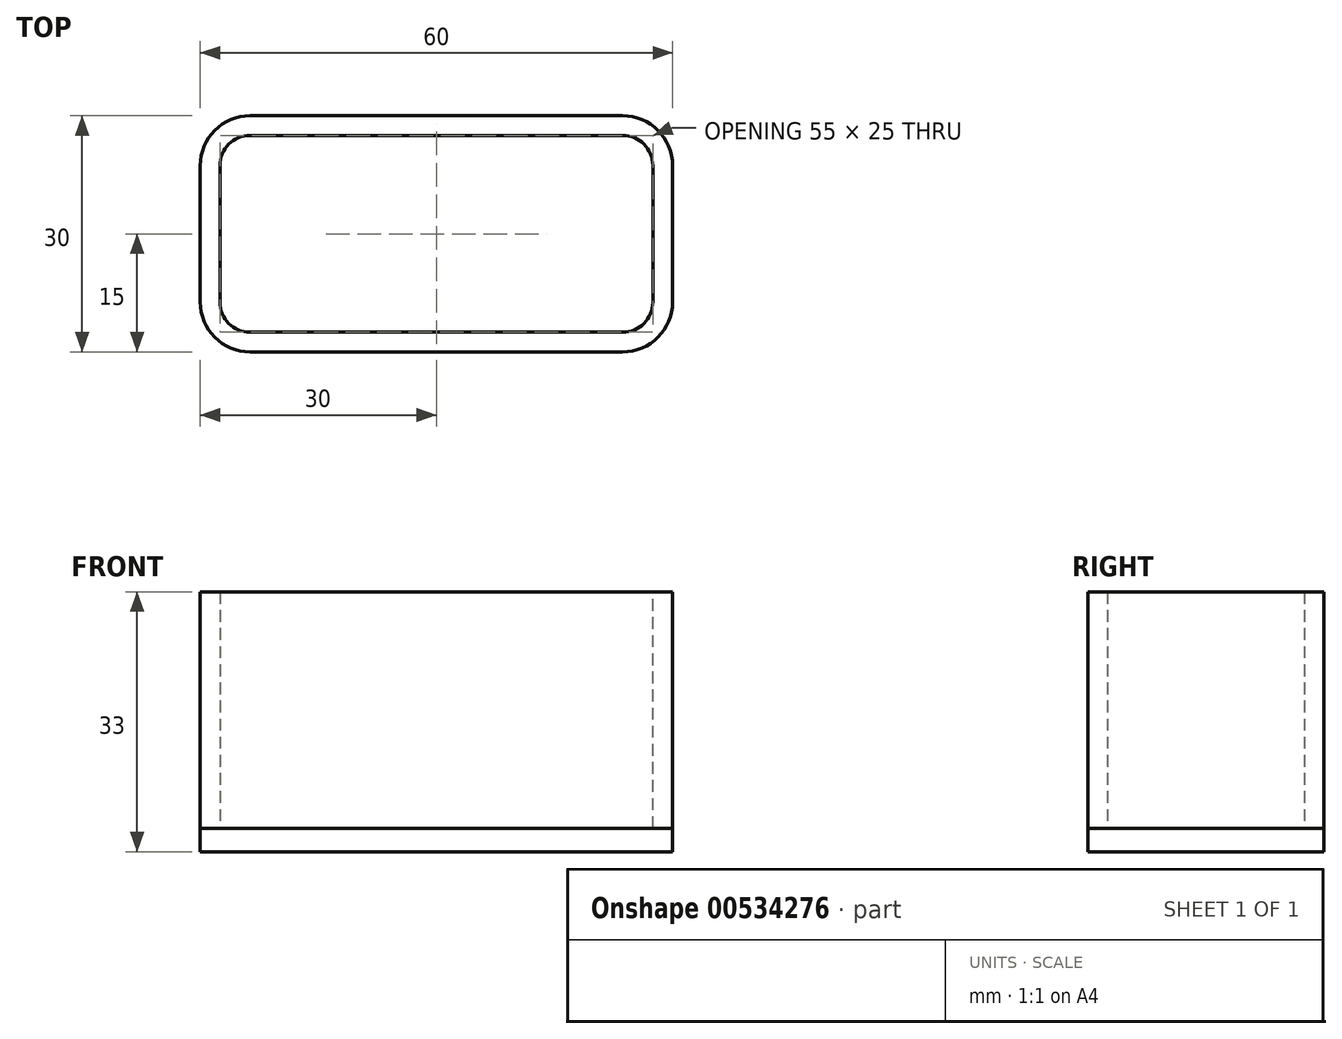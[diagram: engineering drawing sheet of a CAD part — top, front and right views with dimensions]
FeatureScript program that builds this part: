
annotation { "Feature Type Name" : "Feature", "Feature Type Description" : "" }
export const myFeature = defineFeature(function(context is Context, id is Id, definition is map)
    precondition{}
    {
        {
            var Q0;
            Q0=qCreatedBy(makeId("Top.planeOp"),FACE);
            var sketch = newSketch(context, id + "F0", { "sketchPlane" : qUnion([Q0])});
            skLineSegment(sketch, "E0.bottom", {"start": v(23.65, -15) * mm, "end": v(-23.65, -15) * mm});
            skLineSegment(sketch, "E0.top", {"start": v(23.65, 15) * mm, "end": v(-23.65, 15) * mm});
            skLineSegment(sketch, "E0.left", {"start": v(30, -8.65) * mm, "end": v(30, 8.65) * mm});
            skLineSegment(sketch, "E0.right", {"start": v(-30, -8.65) * mm, "end": v(-30, 8.65) * mm});
            skPoint(sketch, "E0.middle", {"position": v(0, 0) * mm});
            skPoint(sketch, "E1.visualSharp", {"position": v(-30, 15) * mm});
            skArc(sketch, "E1.filletArc", {"start": v(-23.65, 15) * mm, "mid": v(-28.14, 13.14) * mm, "end": v(-30, 8.65) * mm});
            skPoint(sketch, "E2.visualSharp", {"position": v(-30, -15) * mm});
            skArc(sketch, "E2.filletArc", {"start": v(-30, -8.65) * mm, "mid": v(-28.14, -13.14) * mm, "end": v(-23.65, -15) * mm});
            skPoint(sketch, "E3.visualSharp", {"position": v(30, -15) * mm});
            skArc(sketch, "E3.filletArc", {"start": v(23.65, -15) * mm, "mid": v(28.14, -13.14) * mm, "end": v(30, -8.65) * mm});
            skPoint(sketch, "E4.visualSharp", {"position": v(30, 15) * mm});
            skArc(sketch, "E4.filletArc", {"start": v(30, 8.65) * mm, "mid": v(28.14, 13.14) * mm, "end": v(23.65, 15) * mm});
            skSolve(sketch);
        }
        {
            var Q0;
            Q0=makeQuery(id+"F0.imprint","IMPRINT",FACE,{"disambiguationData":[TD([[makeQuery(id+"F0.imprint","IMPRINT",EDGE,{"derivedFrom":sQuery(id+"F0.wireOp",EDGE,"E0.bottom")}),-1.0]])]});
            extrude(context, id + "F1", {"entities" : qUnion([Q0]), "depth" : 30 * mm, "offsetDistance" : 25 * mm});
        }
        {
            var Q0;
            Q0=makeQuery(id+"F1.opExtrude","CAP_FACE",FACE,{"disambiguationData":[OSD([sQuery(id+"F0.wireOp",EDGE,"E0.bottom"),sQuery(id+"F0.wireOp",EDGE,"E0.top"),sQuery(id+"F0.wireOp",EDGE,"E0.left"),sQuery(id+"F0.wireOp",EDGE,"E0.right"),sQuery(id+"F0.wireOp",EDGE,"E1.filletArc"),sQuery(id+"F0.wireOp",EDGE,"E2.filletArc"),sQuery(id+"F0.wireOp",EDGE,"E3.filletArc"),sQuery(id+"F0.wireOp",EDGE,"E4.filletArc")])],"isStart":false});
            shell(context, id + "F2", {"entities" : qUnion([Q0]), "thickness" : 2.5 * mm});
        }
        {
            var Q0;
            Q0=makeQuery(id+"F2.opShell","OFFSET_FACE",FACE,{"disambiguationData":[OSD([sQuery(id+"F0.wireOp",EDGE,"E0.bottom"),sQuery(id+"F0.wireOp",EDGE,"E0.top"),sQuery(id+"F0.wireOp",EDGE,"E0.left"),sQuery(id+"F0.wireOp",EDGE,"E0.right"),sQuery(id+"F0.wireOp",EDGE,"E1.filletArc"),sQuery(id+"F0.wireOp",EDGE,"E2.filletArc"),sQuery(id+"F0.wireOp",EDGE,"E3.filletArc"),sQuery(id+"F0.wireOp",EDGE,"E4.filletArc")])]});
            var sketch = newSketch(context, id + "F3", { "sketchPlane" : qUnion([Q0])});
            skArc(sketch, "E5.0.0", {"start": v(27.5, 8.65) * mm, "mid": v(26.37, 11.37) * mm, "end": v(23.65, 12.5) * mm});
            skLineSegment(sketch, "E5.0.1", {"start": v(23.65, 12.5) * mm, "end": v(-23.65, 12.5) * mm});
            skArc(sketch, "E5.0.2", {"start": v(-23.65, 12.5) * mm, "mid": v(-26.37, 11.37) * mm, "end": v(-27.5, 8.65) * mm});
            skLineSegment(sketch, "E5.0.3", {"start": v(-27.5, 8.65) * mm, "end": v(-27.5, -8.65) * mm});
            skArc(sketch, "E5.0.4", {"start": v(-27.5, -8.65) * mm, "mid": v(-26.37, -11.37) * mm, "end": v(-23.65, -12.5) * mm});
            skLineSegment(sketch, "E5.0.5", {"start": v(-23.65, -12.5) * mm, "end": v(23.65, -12.5) * mm});
            skArc(sketch, "E5.0.6", {"start": v(23.65, -12.5) * mm, "mid": v(26.37, -11.37) * mm, "end": v(27.5, -8.65) * mm});
            skLineSegment(sketch, "E5.0.7", {"start": v(27.5, -8.65) * mm, "end": v(27.5, 8.65) * mm});
            skSolve(sketch);
        }
        {
            var Q0;
            Q0 = qSketchRegion(id + "F3", true);
            extrude(context, id + "F4", {"entities" : qUnion([Q0]), "operationType" : NewBodyOperationType.REMOVE, "endBound" : BoundingType.THROUGH_ALL, "oppositeDirection" : true, "depth" : 25 * mm, "offsetDistance" : 25 * mm});
        }
        {
            var Q0;
            Q0 = qSketchRegion(id + "F0", true);
            extrude(context, id + "F5", {"entities" : qUnion([Q0]), "depth" : -3 * mm, "offsetDistance" : 25 * mm});
        }
    });
